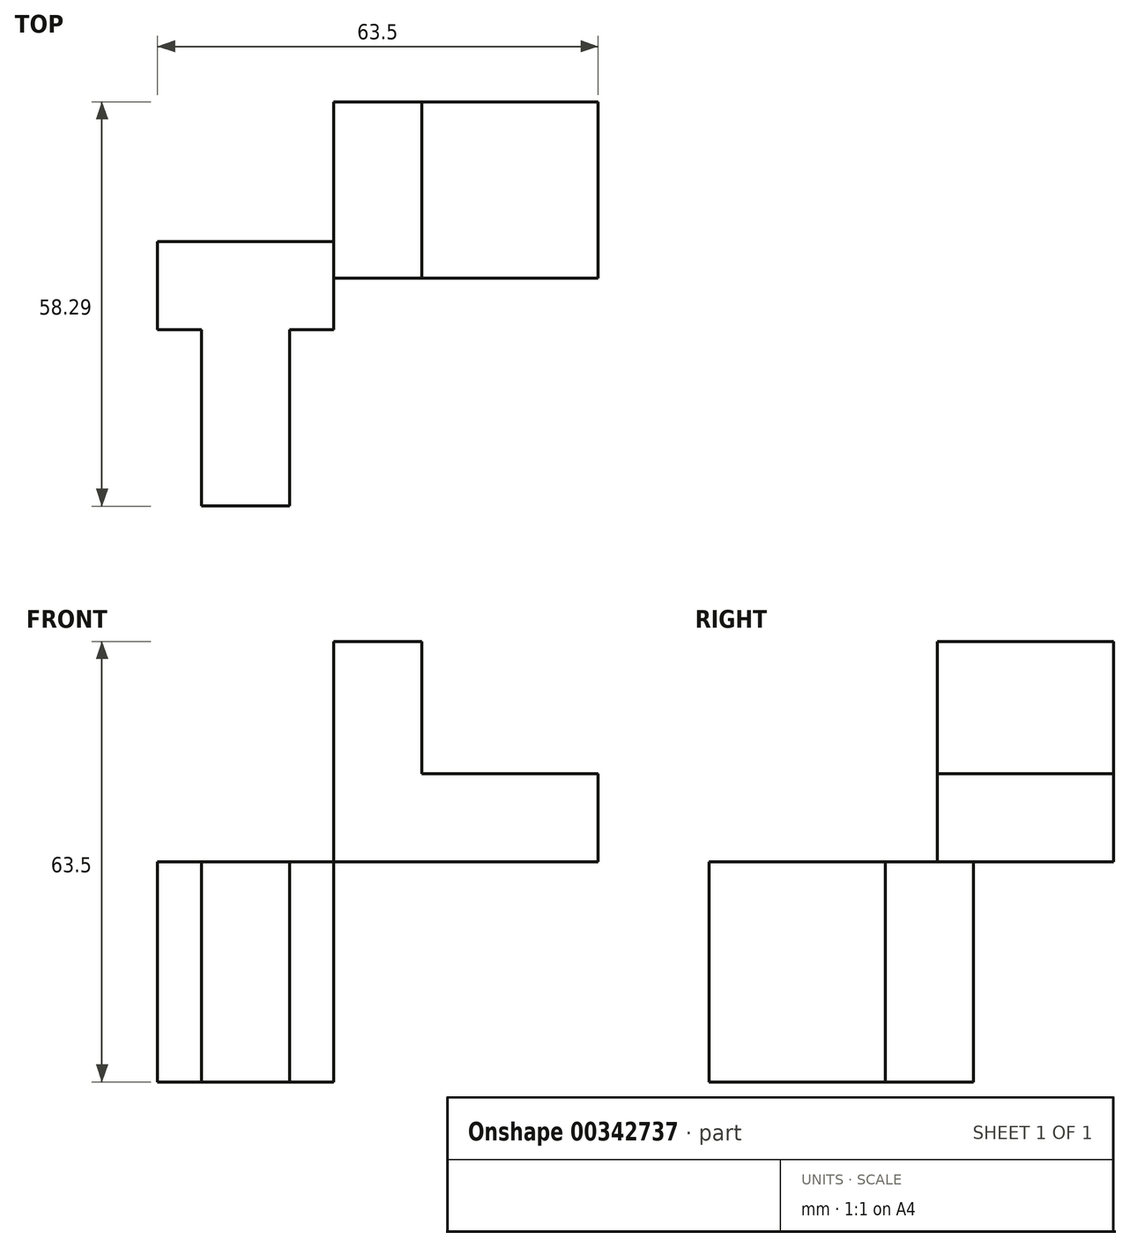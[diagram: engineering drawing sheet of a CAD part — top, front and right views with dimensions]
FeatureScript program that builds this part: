
annotation { "Feature Type Name" : "Feature", "Feature Type Description" : "" }
export const myFeature = defineFeature(function(context is Context, id is Id, definition is map)
    precondition{}
    {
        {
            var Q0;
            Q0=qCreatedBy(makeId("Front.planeOp"),FACE);
            var sketch = newSketch(context, id + "F0", { "sketchPlane" : qUnion([Q0])});
            skLineSegment(sketch, "E0", {"start": v(0, 0) * mm, "end": v(0, 31.75) * mm});
            skLineSegment(sketch, "E1", {"start": v(0, 31.75) * mm, "end": v(12.7, 31.75) * mm});
            skLineSegment(sketch, "E2", {"start": v(12.7, 31.75) * mm, "end": v(12.7, 12.7) * mm});
            skLineSegment(sketch, "E3", {"start": v(12.7, 12.7) * mm, "end": v(38.1, 12.7) * mm});
            skLineSegment(sketch, "E4", {"start": v(38.1, 12.7) * mm, "end": v(38.1, 0) * mm});
            skLineSegment(sketch, "E5", {"start": v(38.1, 0) * mm, "end": v(0, 0) * mm});
            skSolve(sketch);
        }
        {
            var Q0;
            Q0 = qSketchRegion(id + "F0", true);
            extrude(context, id + "F1", {"entities" : qUnion([Q0]), "oppositeDirection" : true, "depth" : 25.4 * mm});
        }
        {
            var Q0;
            Q0=qCreatedBy(makeId("Top.planeOp"),FACE);
            var sketch = newSketch(context, id + "F2", { "sketchPlane" : qUnion([Q0])});
            skLineSegment(sketch, "E6", {"start": v(0, 5.21) * mm, "end": v(-25.4, 5.21) * mm});
            skLineSegment(sketch, "E7", {"start": v(-25.4, 5.21) * mm, "end": v(-25.4, -7.49) * mm});
            skLineSegment(sketch, "E8", {"start": v(-19.05, -7.49) * mm, "end": v(-19.05, -32.89) * mm});
            skLineSegment(sketch, "E9", {"start": v(-19.05, -32.89) * mm, "end": v(-6.35, -32.89) * mm});
            skLineSegment(sketch, "E10", {"start": v(-6.35, -32.89) * mm, "end": v(-6.35, -7.49) * mm});
            skLineSegment(sketch, "E11", {"start": v(-6.35, -7.49) * mm, "end": v(0, -7.49) * mm});
            skLineSegment(sketch, "E12", {"start": v(0, -7.49) * mm, "end": v(0, 5.21) * mm});
            skLineSegment(sketch, "E13", {"start": v(-19.05, -7.49) * mm, "end": v(-25.4, -7.49) * mm});
            skSolve(sketch);
        }
        {
            var Q0;
            Q0 = qSketchRegion(id + "F2", true);
            extrude(context, id + "F3", {"entities" : qUnion([Q0]), "oppositeDirection" : true, "depth" : 31.75 * mm});
        }
    });
